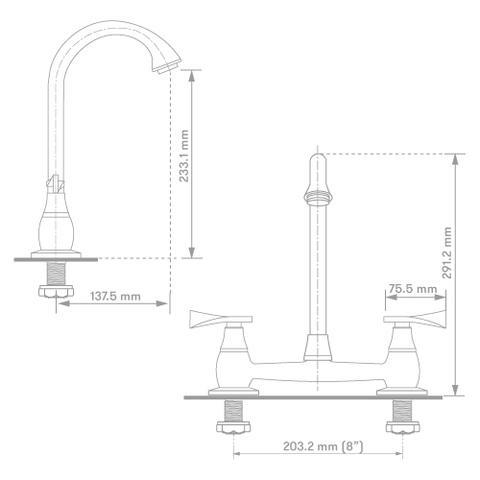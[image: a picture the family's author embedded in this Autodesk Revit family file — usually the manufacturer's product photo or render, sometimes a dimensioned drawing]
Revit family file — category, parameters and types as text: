
# Revit family: 01-2841-11-MEZCLADOR LAVAPLATOS DE MESA PRISTINA
name_source: partatom
category: Plumbing Fixtures
revit_build: Autodesk Revit 2018 (Build: 20170223_1515(x64)
units: mm (PartAtom-declared; Revit-internal decimal feet)

## family parameters
Cut with Voids When Loaded = No
Host = Face
OmniClass Number = 23.31.11.00
Part Type = Normal
Room Calculation Point = No
Round Connector Dimension = Use Diameter
Shared = No

## types (1)
- 01-2841-11
    Alto = 291.2 mm  [stored 0.955381 ft]
    Alto - aireador = 233.1 mm  [stored 0.764764 ft]
    Ancho manija = 75.5 mm
    CW Connection = Yes
    Default Elevation = 0 mm  [stored 0 ft]
    Description = Bimando
    Eje - (roscas) = 203.2 mm
    HW Connection = Yes
    Link Ficha Tecnica = https://infotecnica.gricol.com
    Manufacturer = Gricol
    Metal Laton Cromado = Metal Laton Cromado
    Metal Zamak Cromado = Metal Zamak Cromado
    Model = 01-2841-11
    Plastico - ABS Cromado = Plastico - ABS Cromado
    Product Name = MEZCLADOR LAVAPLATOS DE MESA PRISTINA
    Profundidad = 137.5 mm
    Type Image = 00-FOTO 01-2841-11.jpg
    URL = https://www.gricol.com
    Vent Connection = No
    Waste Connection = No

note: [stored X ft] marks values corroborated as IEEE doubles in the binary element streams (Revit-internal decimal feet)

## geometry (parser evidence)
native form markers: Blend x2, Sweep x5
no freeform markers — native parametric forms only
